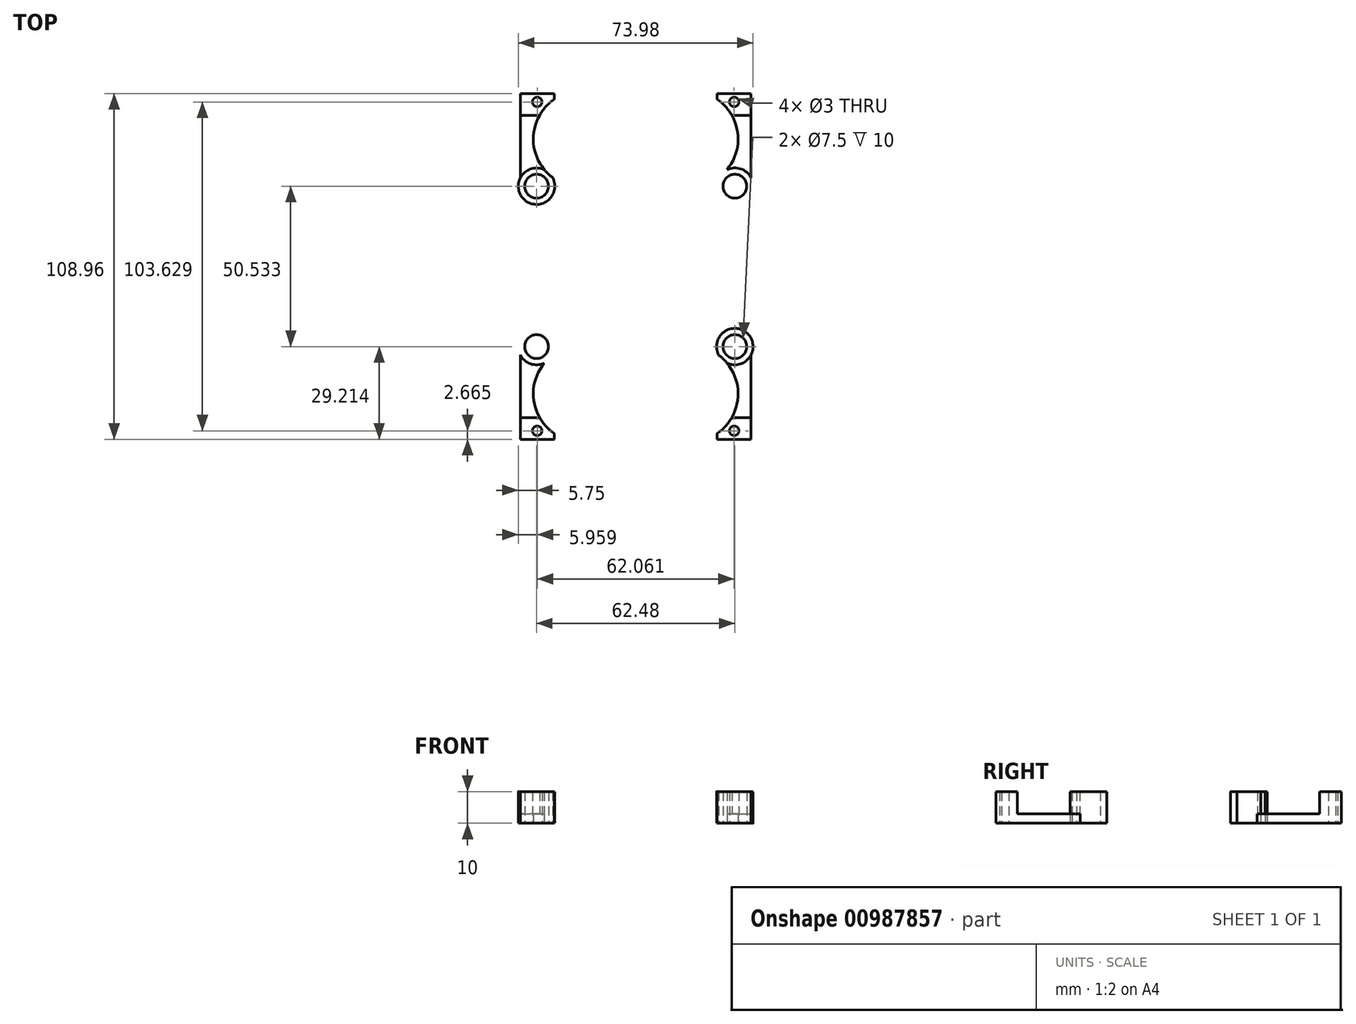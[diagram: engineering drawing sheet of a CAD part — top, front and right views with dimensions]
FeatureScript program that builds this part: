
annotation { "Feature Type Name" : "Feature", "Feature Type Description" : "" }
export const myFeature = defineFeature(function(context is Context, id is Id, definition is map)
    precondition{}
    {
        {
            var Q0;
            Q0=qCreatedBy(makeId("Top.planeOp"),FACE);
            var sketch = newSketch(context, id + "F0", { "sketchPlane" : qUnion([Q0])});
            skCircle(sketch, "E0", {"center": v(-31.24, 25.27) * mm, "radius": 3.75 * mm});
            skCircle(sketch, "E1", {"center": v(-31.24, 25.27) * mm, "radius": 5.75 * mm});
            skCircle(sketch, "E2.MirrorC", {"center": v(31.24, 25.27) * mm, "radius": 3.75 * mm});
            skCircle(sketch, "E3.MirrorC", {"center": v(31.24, 25.27) * mm, "radius": 5.75 * mm});
            skCircle(sketch, "E4.MirrorC", {"center": v(31.24, -25.27) * mm, "radius": 3.75 * mm});
            skCircle(sketch, "E5.MirrorC", {"center": v(31.24, -25.27) * mm, "radius": 5.75 * mm});
            skCircle(sketch, "E6.MirrorC", {"center": v(-31.24, -25.27) * mm, "radius": 3.75 * mm});
            skCircle(sketch, "E7.MirrorC", {"center": v(-31.24, -25.27) * mm, "radius": 5.75 * mm});
            skArc(sketch, "E8", {"start": v(-25.7, 52.64) * mm, "mid": v(-32.26, 40.42) * mm, "end": v(-26.16, 27.96) * mm});
            skLineSegment(sketch, "E9", {"start": v(-36.37, 27.86) * mm, "end": v(-36.37, 54.48) * mm});
            skLineSegment(sketch, "E10", {"start": v(-36.37, 54.48) * mm, "end": v(-25.7, 54.48) * mm});
            skLineSegment(sketch, "E11", {"start": v(-25.7, 54.48) * mm, "end": v(-25.7, 52.64) * mm});
            skArc(sketch, "E12.MirrorCS", {"start": v(25.7, 52.64) * mm, "mid": v(32.26, 40.42) * mm, "end": v(26.16, 27.96) * mm});
            skLineSegment(sketch, "E13.MirrorCS", {"start": v(36.37, 54.48) * mm, "end": v(25.7, 54.48) * mm});
            skLineSegment(sketch, "E14.MirrorCS", {"start": v(36.37, 27.86) * mm, "end": v(36.37, 54.48) * mm});
            skArc(sketch, "E15.MirrorCS", {"start": v(25.7, -52.64) * mm, "mid": v(32.26, -40.42) * mm, "end": v(26.16, -27.96) * mm});
            skLineSegment(sketch, "E16.MirrorCS", {"start": v(36.37, -27.86) * mm, "end": v(36.37, -54.48) * mm});
            skLineSegment(sketch, "E17.MirrorCS", {"start": v(36.37, -54.48) * mm, "end": v(25.7, -54.48) * mm});
            skArc(sketch, "E18.MirrorCS", {"start": v(-25.7, -52.64) * mm, "mid": v(-32.26, -40.42) * mm, "end": v(-26.16, -27.96) * mm});
            skLineSegment(sketch, "E19.MirrorCS", {"start": v(-36.37, -27.86) * mm, "end": v(-36.37, -54.48) * mm});
            skLineSegment(sketch, "E20.MirrorCS", {"start": v(-36.37, -54.48) * mm, "end": v(-25.7, -54.48) * mm});
            skLineSegment(sketch, "E21", {"start": v(25.7, 52.64) * mm, "end": v(25.7, 54.48) * mm});
            skLineSegment(sketch, "E22", {"start": v(25.7, 54.48) * mm, "end": v(25.7, 52.64) * mm});
            skLineSegment(sketch, "E23", {"start": v(25.7, -52.64) * mm, "end": v(25.7, -54.48) * mm});
            skLineSegment(sketch, "E24", {"start": v(-25.7, -54.48) * mm, "end": v(-25.7, -52.64) * mm});
            skLineSegment(sketch, "E25", {"start": v(-36.37, 47.63) * mm, "end": v(-30.29, 47.63) * mm});
            skLineSegment(sketch, "E26.MirrorCS", {"start": v(36.37, 47.63) * mm, "end": v(30.29, 47.63) * mm});
            skLineSegment(sketch, "E27.MirrorCS", {"start": v(-36.37, -47.63) * mm, "end": v(-30.29, -47.63) * mm});
            skLineSegment(sketch, "E28.MirrorCS", {"start": v(36.37, -47.63) * mm, "end": v(30.29, -47.63) * mm});
            skPoint(sketch, "E29.centerSnap0", {"position": v(-31.03, 54.48) * mm});
            skCircle(sketch, "E30", {"center": v(-31.03, 51.81) * mm, "radius": 1.5 * mm});
            skCircle(sketch, "E31.MirrorC", {"center": v(31.03, 51.81) * mm, "radius": 1.5 * mm});
            skCircle(sketch, "E32.MirrorC", {"center": v(31.03, -51.81) * mm, "radius": 1.5 * mm});
            skCircle(sketch, "E33.MirrorC", {"center": v(-31.03, -51.81) * mm, "radius": 1.5 * mm});
            skSolve(sketch);
        }
        {
            var Q0;
            Q0=makeQuery(id+"F0.imprint","IMPRINT",FACE,{"disambiguationData":[TD([[makeQuery(id+"F0.imprint","IMPRINT",EDGE,{"derivedFrom":sQuery(id+"F0.wireOp",EDGE,"E0")}),-1.0]])]});
            var Q1;
            Q1=makeQuery(id+"F0.imprint","IMPRINT",FACE,{"disambiguationData":[TD([[makeQuery(id+"F0.imprint","IMPRINT",EDGE,{"derivedFrom":sQuery(id+"F0.wireOp",EDGE,"E2.MirrorC")}),1.0]])]});
            var Q2;
            Q2=makeQuery(id+"F0.imprint","IMPRINT",FACE,{"disambiguationData":[TD([[makeQuery(id+"F0.imprint","IMPRINT",EDGE,{"derivedFrom":sQuery(id+"F0.wireOp",EDGE,"E13.MirrorCS")}),1.0]])]});
            var Q3;
            Q3=makeQuery(id+"F0.imprint","IMPRINT",FACE,{"disambiguationData":[TD([[makeQuery(id+"F0.imprint","IMPRINT",EDGE,{"derivedFrom":sQuery(id+"F0.wireOp",EDGE,"E4.MirrorC")}),-1.0]])]});
            var Q4;
            {var subQ0=sQuery(id+"F0.wireOp",EDGE,"E16.MirrorCS");Q4=makeQuery(id+"F0.imprint","IMPRINT",FACE,{"disambiguationData":[TD([[makeQuery(id+"F0.imprint","IMPRINT",EDGE,{"derivedFrom":subQ0}),-1.0]])]});}
            var Q5;
            Q5=makeQuery(id+"F0.imprint","IMPRINT",FACE,{"disambiguationData":[TD([[makeQuery(id+"F0.imprint","IMPRINT",EDGE,{"derivedFrom":sQuery(id+"F0.wireOp",EDGE,"E6.MirrorC")}),1.0]])]});
            var Q6;
            {var subQ0=sQuery(id+"F0.wireOp",EDGE,"E9");Q6=makeQuery(id+"F0.imprint","IMPRINT",FACE,{"disambiguationData":[TD([[makeQuery(id+"F0.imprint","IMPRINT",EDGE,{"derivedFrom":subQ0}),-1.0]])]});}
            var Q7;
            {var subQ0=sQuery(id+"F0.wireOp",EDGE,"E19.MirrorCS");Q7=makeQuery(id+"F0.imprint","IMPRINT",FACE,{"disambiguationData":[TD([[makeQuery(id+"F0.imprint","IMPRINT",EDGE,{"derivedFrom":subQ0}),1.0]])]});}
            var Q8;
            {var subQ5=sQuery(id+"F0.wireOp",EDGE,"E26.MirrorCS");Q8=makeQuery(id+"F0.imprint","IMPRINT",FACE,{"disambiguationData":[TD([[makeQuery(id+"F0.imprint","IMPRINT",EDGE,{"derivedFrom":subQ5}),1.0]])]});}
            var Q9;
            {var subQ2=sQuery(id+"F0.wireOp",EDGE,"E10");Q9=makeQuery(id+"F0.imprint","IMPRINT",FACE,{"disambiguationData":[TD([[makeQuery(id+"F0.imprint","IMPRINT",EDGE,{"derivedFrom":subQ2}),-1.0]])]});}
            var Q10;
            {var subQ1=sQuery(id+"F0.wireOp",EDGE,"E17.MirrorCS");Q10=makeQuery(id+"F0.imprint","IMPRINT",FACE,{"disambiguationData":[TD([[makeQuery(id+"F0.imprint","IMPRINT",EDGE,{"derivedFrom":subQ1}),-1.0]])]});}
            var Q11;
            {var subQ1=sQuery(id+"F0.wireOp",EDGE,"E20.MirrorCS");Q11=makeQuery(id+"F0.imprint","IMPRINT",FACE,{"disambiguationData":[TD([[makeQuery(id+"F0.imprint","IMPRINT",EDGE,{"derivedFrom":subQ1}),1.0]])]});}
            extrude(context, id + "F1", {"entities" : qUnion([Q0, Q1, Q2, Q3, Q4, Q5, Q6, Q7, Q8, Q9, Q10, Q11]), "depth" : 3 * mm, "offsetDistance" : 25 * mm});
        }
        {
            var Q0;
            Q0=makeQuery(id+"F0.imprint","IMPRINT",FACE,{"disambiguationData":[TD([[makeQuery(id+"F0.imprint","IMPRINT",EDGE,{"derivedFrom":sQuery(id+"F0.wireOp",EDGE,"E0")}),-1.0]])]});
            var Q1;
            Q1=makeQuery(id+"F0.imprint","IMPRINT",FACE,{"disambiguationData":[TD([[makeQuery(id+"F0.imprint","IMPRINT",EDGE,{"derivedFrom":sQuery(id+"F0.wireOp",EDGE,"E2.MirrorC")}),1.0]])]});
            var Q2;
            Q2=makeQuery(id+"F0.imprint","IMPRINT",FACE,{"disambiguationData":[TD([[makeQuery(id+"F0.imprint","IMPRINT",EDGE,{"derivedFrom":sQuery(id+"F0.wireOp",EDGE,"E4.MirrorC")}),-1.0]])]});
            var Q3;
            Q3=makeQuery(id+"F0.imprint","IMPRINT",FACE,{"disambiguationData":[TD([[makeQuery(id+"F0.imprint","IMPRINT",EDGE,{"derivedFrom":sQuery(id+"F0.wireOp",EDGE,"E6.MirrorC")}),1.0]])]});
            var Q4;
            {var subQ2=sQuery(id+"F0.wireOp",EDGE,"E10");Q4=makeQuery(id+"F0.imprint","IMPRINT",FACE,{"disambiguationData":[TD([[makeQuery(id+"F0.imprint","IMPRINT",EDGE,{"derivedFrom":subQ2}),-1.0]])]});}
            var Q5;
            {var subQ1=sQuery(id+"F0.wireOp",EDGE,"E13.MirrorCS");Q5=makeQuery(id+"F0.imprint","IMPRINT",FACE,{"disambiguationData":[TD([[makeQuery(id+"F0.imprint","IMPRINT",EDGE,{"derivedFrom":subQ1}),1.0]])]});}
            var Q6;
            {var subQ1=sQuery(id+"F0.wireOp",EDGE,"E17.MirrorCS");Q6=makeQuery(id+"F0.imprint","IMPRINT",FACE,{"disambiguationData":[TD([[makeQuery(id+"F0.imprint","IMPRINT",EDGE,{"derivedFrom":subQ1}),-1.0]])]});}
            var Q7;
            {var subQ1=sQuery(id+"F0.wireOp",EDGE,"E20.MirrorCS");Q7=makeQuery(id+"F0.imprint","IMPRINT",FACE,{"disambiguationData":[TD([[makeQuery(id+"F0.imprint","IMPRINT",EDGE,{"derivedFrom":subQ1}),1.0]])]});}
            extrude(context, id + "F2", {"entities" : qUnion([Q0, Q1, Q2, Q3, Q4, Q5, Q6, Q7]), "operationType" : NewBodyOperationType.ADD, "depth" : 10 * mm, "offsetDistance" : 25 * mm});
        }
    });
